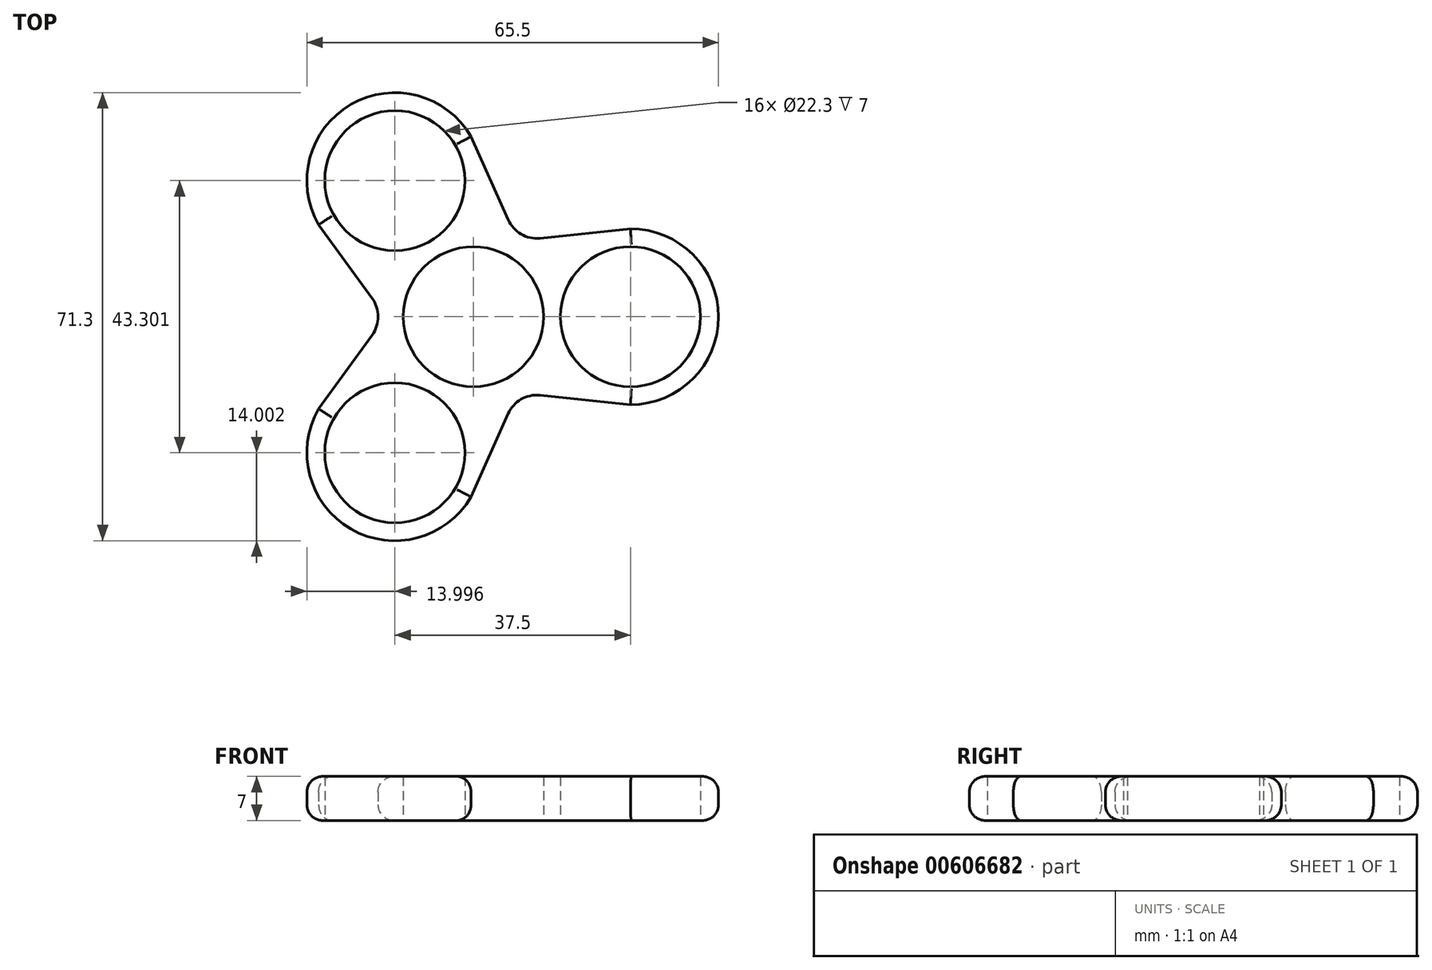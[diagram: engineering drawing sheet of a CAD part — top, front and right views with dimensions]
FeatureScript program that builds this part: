
annotation { "Feature Type Name" : "Feature", "Feature Type Description" : "" }
export const myFeature = defineFeature(function(context is Context, id is Id, definition is map)
    precondition{}
    {
        {
            var Q0;
            Q0=qCreatedBy(makeId("Top.planeOp"),FACE);
            var sketch = newSketch(context, id + "F0", { "sketchPlane" : qUnion([Q0])});
            skCircle(sketch, "E0", {"center": v(-126.34, 8.47) * mm, "radius": 14 * mm});
            skLineSegment(sketch, "E1", {"start": v(-126.34, 8.47) * mm, "end": v(-101.34, 8.47) * mm});
            skLineSegment(sketch, "E2", {"start": v(-126.34, 8.47) * mm, "end": v(-138.84, 30.12) * mm});
            skLineSegment(sketch, "E3", {"start": v(-126.34, 8.47) * mm, "end": v(-138.84, -13.18) * mm});
            skCircle(sketch, "E4", {"center": v(-138.84, 30.12) * mm, "radius": 14 * mm});
            skCircle(sketch, "E5", {"center": v(-101.34, 8.47) * mm, "radius": 14 * mm});
            skCircle(sketch, "E6", {"center": v(-138.84, -13.18) * mm, "radius": 14 * mm});
            skCircle(sketch, "E7", {"center": v(-138.84, 30.12) * mm, "radius": 11.15 * mm});
            skCircle(sketch, "E8", {"center": v(-101.34, 8.47) * mm, "radius": 11.15 * mm});
            skCircle(sketch, "E9", {"center": v(-138.84, -13.18) * mm, "radius": 11.15 * mm});
            skCircle(sketch, "E10", {"center": v(-126.34, 8.47) * mm, "radius": 11.15 * mm});
            skLineSegment(sketch, "E11", {"start": v(-126.34, 8.47) * mm, "end": v(-119.34, -3.65) * mm});
            skLineSegment(sketch, "E12", {"start": v(-126.34, 8.47) * mm, "end": v(-140.34, 8.47) * mm});
            skLineSegment(sketch, "E13", {"start": v(-126.34, 8.47) * mm, "end": v(-119.34, 20.6) * mm});
            skLineSegment(sketch, "E14", {"start": v(-138.84, -13.18) * mm, "end": v(-126.72, -20.18) * mm});
            skLineSegment(sketch, "E15", {"start": v(-138.84, -13.18) * mm, "end": v(-150.97, -6.18) * mm});
            skLineSegment(sketch, "E16", {"start": v(-101.34, 8.47) * mm, "end": v(-101.34, -5.53) * mm});
            skLineSegment(sketch, "E17", {"start": v(-101.34, 8.47) * mm, "end": v(-101.34, 22.47) * mm});
            skLineSegment(sketch, "E18", {"start": v(-138.84, 30.12) * mm, "end": v(-126.72, 37.12) * mm});
            skLineSegment(sketch, "E19", {"start": v(-138.84, 30.12) * mm, "end": v(-150.97, 23.12) * mm});
            skLineSegment(sketch, "E20", {"start": v(-126.72, -20.18) * mm, "end": v(-119.34, -3.65) * mm});
            skLineSegment(sketch, "E21", {"start": v(-150.97, -6.18) * mm, "end": v(-140.34, 8.47) * mm});
            skLineSegment(sketch, "E22", {"start": v(-150.97, 23.12) * mm, "end": v(-140.34, 8.47) * mm});
            skLineSegment(sketch, "E23", {"start": v(-126.72, 37.12) * mm, "end": v(-119.34, 20.6) * mm});
            skLineSegment(sketch, "E24", {"start": v(-101.34, -5.53) * mm, "end": v(-119.34, -3.65) * mm});
            skLineSegment(sketch, "E25", {"start": v(-101.34, 22.47) * mm, "end": v(-119.34, 20.6) * mm});
            skSolve(sketch);
        }
        {
            var Q0;
            {var subQ3=sQuery(id+"F0.wireOp",EDGE,"E19");var subQ5=sQuery(id+"F0.wireOp",EDGE,"E7");var subQ6=makeQuery(id+"F0.imprint","INTERSECT",VERTEX,{"derivedFrom":[subQ5,subQ3]});Q0=makeQuery(id+"F0.imprint","IMPRINT",FACE,{"disambiguationData":[TD([[makeQuery(id+"F0.imprint","IMPRINT",EDGE,{"disambiguationData":[TD([[subQ6,1.0]])],"derivedFrom":subQ5}),-1.0]])]});}
            var Q1;
            {var subQ5=sQuery(id+"F0.wireOp",EDGE,"E23");var subQ6=sQuery(id+"F0.wireOp",EDGE,"E4");var subQ8=makeQuery(id+"F0.imprint","INTERSECT",VERTEX,{"derivedFrom":[subQ6,subQ5]});Q1=makeQuery(id+"F0.imprint","IMPRINT",FACE,{"disambiguationData":[TD([[makeQuery(id+"F0.imprint","IMPRINT",EDGE,{"disambiguationData":[TD([[subQ8,1.0]])],"derivedFrom":subQ6}),1.0]])]});}
            var Q2;
            {var subQ5=sQuery(id+"F0.wireOp",EDGE,"E22");var subQ6=sQuery(id+"F0.wireOp",EDGE,"E4");var subQ8=makeQuery(id+"F0.imprint","INTERSECT",VERTEX,{"derivedFrom":[subQ6,subQ5]});Q2=makeQuery(id+"F0.imprint","IMPRINT",FACE,{"disambiguationData":[TD([[makeQuery(id+"F0.imprint","IMPRINT",EDGE,{"disambiguationData":[TD([[subQ8,-1.0]])],"derivedFrom":subQ6}),1.0]])]});}
            var Q3;
            {var subQ0=sQuery(id+"F0.wireOp",EDGE,"E4");var subQ1=sQuery(id+"F0.wireOp",EDGE,"E0");var subQ2=makeQuery(id+"F0.imprint","INTERSECT",VERTEX,{"disambiguationData":[OD(1.0)],"derivedFrom":[subQ1,subQ0]});Q3=makeQuery(id+"F0.imprint","IMPRINT",FACE,{"disambiguationData":[TD([[makeQuery(id+"F0.imprint","IMPRINT",EDGE,{"disambiguationData":[TD([[subQ2,1.0]])],"derivedFrom":subQ1}),1.0]])]});}
            var Q4;
            {var subQ0=sQuery(id+"F0.wireOp",EDGE,"E4");var subQ1=sQuery(id+"F0.wireOp",EDGE,"E0");var subQ2=makeQuery(id+"F0.imprint","INTERSECT",VERTEX,{"disambiguationData":[OD(0.0)],"derivedFrom":[subQ1,subQ0]});Q4=makeQuery(id+"F0.imprint","IMPRINT",FACE,{"disambiguationData":[TD([[makeQuery(id+"F0.imprint","IMPRINT",EDGE,{"disambiguationData":[TD([[subQ2,-1.0]])],"derivedFrom":subQ1}),1.0]])]});}
            var Q5;
            {var subQ1=sQuery(id+"F0.wireOp",EDGE,"E0");var subQ3=sQuery(id+"F0.wireOp",EDGE,"E4");var subQ4=makeQuery(id+"F0.imprint","INTERSECT",VERTEX,{"disambiguationData":[OD(0.0)],"derivedFrom":[subQ1,subQ3]});Q5=makeQuery(id+"F0.imprint","IMPRINT",FACE,{"disambiguationData":[TD([[makeQuery(id+"F0.imprint","IMPRINT",EDGE,{"disambiguationData":[TD([[subQ4,1.0]])],"derivedFrom":subQ3}),-1.0]])]});}
            var Q6;
            {var subQ1=sQuery(id+"F0.wireOp",EDGE,"E0");var subQ3=sQuery(id+"F0.wireOp",EDGE,"E4");var subQ4=makeQuery(id+"F0.imprint","INTERSECT",VERTEX,{"disambiguationData":[OD(1.0)],"derivedFrom":[subQ1,subQ3]});Q6=makeQuery(id+"F0.imprint","IMPRINT",FACE,{"disambiguationData":[TD([[makeQuery(id+"F0.imprint","IMPRINT",EDGE,{"disambiguationData":[TD([[subQ4,-1.0]])],"derivedFrom":subQ3}),-1.0]])]});}
            var Q7;
            {var subQ1=sQuery(id+"F0.wireOp",EDGE,"E0");var subQ3=sQuery(id+"F0.wireOp",EDGE,"E6");var subQ4=makeQuery(id+"F0.imprint","INTERSECT",VERTEX,{"disambiguationData":[OD(0.0)],"derivedFrom":[subQ1,subQ3]});Q7=makeQuery(id+"F0.imprint","IMPRINT",FACE,{"disambiguationData":[TD([[makeQuery(id+"F0.imprint","IMPRINT",EDGE,{"disambiguationData":[TD([[subQ4,1.0]])],"derivedFrom":subQ3}),-1.0]])]});}
            var Q8;
            {var subQ0=sQuery(id+"F0.wireOp",EDGE,"E21");var subQ2=sQuery(id+"F0.wireOp",EDGE,"E6");var subQ6=makeQuery(id+"F0.imprint","INTERSECT",VERTEX,{"derivedFrom":[subQ2,subQ0]});Q8=makeQuery(id+"F0.imprint","IMPRINT",FACE,{"disambiguationData":[TD([[makeQuery(id+"F0.imprint","IMPRINT",EDGE,{"disambiguationData":[TD([[subQ6,1.0]])],"derivedFrom":subQ2}),1.0]])]});}
            var Q9;
            {var subQ0=sQuery(id+"F0.wireOp",EDGE,"E6");var subQ1=sQuery(id+"F0.wireOp",EDGE,"E0");var subQ2=makeQuery(id+"F0.imprint","INTERSECT",VERTEX,{"disambiguationData":[OD(0.0)],"derivedFrom":[subQ1,subQ0]});Q9=makeQuery(id+"F0.imprint","IMPRINT",FACE,{"disambiguationData":[TD([[makeQuery(id+"F0.imprint","IMPRINT",EDGE,{"disambiguationData":[TD([[subQ2,-1.0]])],"derivedFrom":subQ1}),1.0]])]});}
            var Q10;
            {var subQ0=sQuery(id+"F0.wireOp",EDGE,"E6");var subQ1=sQuery(id+"F0.wireOp",EDGE,"E0");var subQ2=makeQuery(id+"F0.imprint","INTERSECT",VERTEX,{"disambiguationData":[OD(1.0)],"derivedFrom":[subQ1,subQ0]});Q10=makeQuery(id+"F0.imprint","IMPRINT",FACE,{"disambiguationData":[TD([[makeQuery(id+"F0.imprint","IMPRINT",EDGE,{"disambiguationData":[TD([[subQ2,1.0]])],"derivedFrom":subQ1}),1.0]])]});}
            var Q11;
            {var subQ1=sQuery(id+"F0.wireOp",EDGE,"E0");var subQ3=sQuery(id+"F0.wireOp",EDGE,"E6");var subQ4=makeQuery(id+"F0.imprint","INTERSECT",VERTEX,{"disambiguationData":[OD(1.0)],"derivedFrom":[subQ1,subQ3]});Q11=makeQuery(id+"F0.imprint","IMPRINT",FACE,{"disambiguationData":[TD([[makeQuery(id+"F0.imprint","IMPRINT",EDGE,{"disambiguationData":[TD([[subQ4,-1.0]])],"derivedFrom":subQ3}),-1.0]])]});}
            var Q12;
            {var subQ1=sQuery(id+"F0.wireOp",EDGE,"E0");var subQ3=sQuery(id+"F0.wireOp",EDGE,"E5");var subQ4=makeQuery(id+"F0.imprint","INTERSECT",VERTEX,{"disambiguationData":[OD(1.0)],"derivedFrom":[subQ1,subQ3]});Q12=makeQuery(id+"F0.imprint","IMPRINT",FACE,{"disambiguationData":[TD([[makeQuery(id+"F0.imprint","IMPRINT",EDGE,{"disambiguationData":[TD([[subQ4,1.0]])],"derivedFrom":subQ3}),-1.0]])]});}
            var Q13;
            {var subQ0=sQuery(id+"F0.wireOp",EDGE,"E5");var subQ1=sQuery(id+"F0.wireOp",EDGE,"E0");var subQ2=makeQuery(id+"F0.imprint","INTERSECT",VERTEX,{"disambiguationData":[OD(1.0)],"derivedFrom":[subQ1,subQ0]});Q13=makeQuery(id+"F0.imprint","IMPRINT",FACE,{"disambiguationData":[TD([[makeQuery(id+"F0.imprint","IMPRINT",EDGE,{"disambiguationData":[TD([[subQ2,-1.0]])],"derivedFrom":subQ1}),1.0]])]});}
            var Q14;
            {var subQ0=sQuery(id+"F0.wireOp",EDGE,"E5");var subQ1=sQuery(id+"F0.wireOp",EDGE,"E0");var subQ2=makeQuery(id+"F0.imprint","INTERSECT",VERTEX,{"disambiguationData":[OD(0.0)],"derivedFrom":[subQ1,subQ0]});Q14=makeQuery(id+"F0.imprint","IMPRINT",FACE,{"disambiguationData":[TD([[makeQuery(id+"F0.imprint","IMPRINT",EDGE,{"disambiguationData":[TD([[subQ2,1.0]])],"derivedFrom":subQ1}),1.0]])]});}
            var Q15;
            {var subQ1=sQuery(id+"F0.wireOp",EDGE,"E0");var subQ3=sQuery(id+"F0.wireOp",EDGE,"E5");var subQ4=makeQuery(id+"F0.imprint","INTERSECT",VERTEX,{"disambiguationData":[OD(0.0)],"derivedFrom":[subQ1,subQ3]});Q15=makeQuery(id+"F0.imprint","IMPRINT",FACE,{"disambiguationData":[TD([[makeQuery(id+"F0.imprint","IMPRINT",EDGE,{"disambiguationData":[TD([[subQ4,-1.0]])],"derivedFrom":subQ3}),-1.0]])]});}
            var Q16;
            {var subQ0=sQuery(id+"F0.wireOp",EDGE,"E20");var subQ2=sQuery(id+"F0.wireOp",EDGE,"E6");var subQ6=makeQuery(id+"F0.imprint","INTERSECT",VERTEX,{"derivedFrom":[subQ2,subQ0]});Q16=makeQuery(id+"F0.imprint","IMPRINT",FACE,{"disambiguationData":[TD([[makeQuery(id+"F0.imprint","IMPRINT",EDGE,{"disambiguationData":[TD([[subQ6,-1.0]])],"derivedFrom":subQ2}),1.0]])]});}
            var Q17;
            {var subQ3=sQuery(id+"F0.wireOp",EDGE,"E15");var subQ5=sQuery(id+"F0.wireOp",EDGE,"E9");var subQ6=makeQuery(id+"F0.imprint","INTERSECT",VERTEX,{"derivedFrom":[subQ5,subQ3]});Q17=makeQuery(id+"F0.imprint","IMPRINT",FACE,{"disambiguationData":[TD([[makeQuery(id+"F0.imprint","IMPRINT",EDGE,{"disambiguationData":[TD([[subQ6,-1.0]])],"derivedFrom":subQ5}),-1.0]])]});}
            var Q18;
            {var subQ0=sQuery(id+"F0.wireOp",EDGE,"E24");var subQ2=sQuery(id+"F0.wireOp",EDGE,"E5");var subQ8=makeQuery(id+"F0.imprint","INTERSECT",VERTEX,{"derivedFrom":[subQ2,subQ0]});Q18=makeQuery(id+"F0.imprint","IMPRINT",FACE,{"disambiguationData":[TD([[makeQuery(id+"F0.imprint","IMPRINT",EDGE,{"disambiguationData":[TD([[subQ8,1.0]])],"derivedFrom":subQ2}),1.0]])]});}
            var Q19;
            {var subQ0=sQuery(id+"F0.wireOp",EDGE,"E25");var subQ1=sQuery(id+"F0.wireOp",EDGE,"E5");var subQ2=makeQuery(id+"F0.imprint","INTERSECT",VERTEX,{"derivedFrom":[subQ1,subQ0]});Q19=makeQuery(id+"F0.imprint","IMPRINT",FACE,{"disambiguationData":[TD([[makeQuery(id+"F0.imprint","IMPRINT",EDGE,{"disambiguationData":[TD([[subQ2,-1.0]])],"derivedFrom":subQ1}),1.0]])]});}
            var Q20;
            {var subQ3=sQuery(id+"F0.wireOp",EDGE,"E17");var subQ5=sQuery(id+"F0.wireOp",EDGE,"E8");var subQ6=makeQuery(id+"F0.imprint","INTERSECT",VERTEX,{"derivedFrom":[subQ5,subQ3]});Q20=makeQuery(id+"F0.imprint","IMPRINT",FACE,{"disambiguationData":[TD([[makeQuery(id+"F0.imprint","IMPRINT",EDGE,{"disambiguationData":[TD([[subQ6,1.0]])],"derivedFrom":subQ5}),-1.0]])]});}
            var Q21;
            {var subQ0=sQuery(id+"F0.wireOp",EDGE,"E22");var subQ3=sQuery(id+"F0.wireOp",EDGE,"E4");var subQ5=makeQuery(id+"F0.imprint","INTERSECT",VERTEX,{"derivedFrom":[subQ3,subQ0]});Q21=makeQuery(id+"F0.imprint","IMPRINT",FACE,{"disambiguationData":[TD([[makeQuery(id+"F0.imprint","IMPRINT",EDGE,{"disambiguationData":[TD([[subQ5,-1.0]])],"derivedFrom":subQ3}),-1.0]])]});}
            var Q22;
            {var subQ0=sQuery(id+"F0.wireOp",EDGE,"E21");var subQ3=sQuery(id+"F0.wireOp",EDGE,"E6");var subQ5=makeQuery(id+"F0.imprint","INTERSECT",VERTEX,{"derivedFrom":[subQ3,subQ0]});Q22=makeQuery(id+"F0.imprint","IMPRINT",FACE,{"disambiguationData":[TD([[makeQuery(id+"F0.imprint","IMPRINT",EDGE,{"disambiguationData":[TD([[subQ5,1.0]])],"derivedFrom":subQ3}),-1.0]])]});}
            var Q23;
            {var subQ0=sQuery(id+"F0.wireOp",EDGE,"E20");var subQ3=sQuery(id+"F0.wireOp",EDGE,"E6");var subQ5=makeQuery(id+"F0.imprint","INTERSECT",VERTEX,{"derivedFrom":[subQ3,subQ0]});Q23=makeQuery(id+"F0.imprint","IMPRINT",FACE,{"disambiguationData":[TD([[makeQuery(id+"F0.imprint","IMPRINT",EDGE,{"disambiguationData":[TD([[subQ5,-1.0]])],"derivedFrom":subQ3}),-1.0]])]});}
            var Q24;
            {var subQ0=sQuery(id+"F0.wireOp",EDGE,"E24");var subQ3=sQuery(id+"F0.wireOp",EDGE,"E5");var subQ5=makeQuery(id+"F0.imprint","INTERSECT",VERTEX,{"derivedFrom":[subQ3,subQ0]});Q24=makeQuery(id+"F0.imprint","IMPRINT",FACE,{"disambiguationData":[TD([[makeQuery(id+"F0.imprint","IMPRINT",EDGE,{"disambiguationData":[TD([[subQ5,1.0]])],"derivedFrom":subQ3}),-1.0]])]});}
            var Q25;
            {var subQ0=sQuery(id+"F0.wireOp",EDGE,"E25");var subQ3=sQuery(id+"F0.wireOp",EDGE,"E5");var subQ5=makeQuery(id+"F0.imprint","INTERSECT",VERTEX,{"derivedFrom":[subQ3,subQ0]});Q25=makeQuery(id+"F0.imprint","IMPRINT",FACE,{"disambiguationData":[TD([[makeQuery(id+"F0.imprint","IMPRINT",EDGE,{"disambiguationData":[TD([[subQ5,-1.0]])],"derivedFrom":subQ3}),-1.0]])]});}
            var Q26;
            {var subQ0=sQuery(id+"F0.wireOp",EDGE,"E23");var subQ3=sQuery(id+"F0.wireOp",EDGE,"E4");var subQ5=makeQuery(id+"F0.imprint","INTERSECT",VERTEX,{"derivedFrom":[subQ3,subQ0]});Q26=makeQuery(id+"F0.imprint","IMPRINT",FACE,{"disambiguationData":[TD([[makeQuery(id+"F0.imprint","IMPRINT",EDGE,{"disambiguationData":[TD([[subQ5,1.0]])],"derivedFrom":subQ3}),-1.0]])]});}
            extrude(context, id + "F1", {"entities" : qUnion([Q0, Q1, Q2, Q3, Q4, Q5, Q6, Q7, Q8, Q9, Q10, Q11, Q12, Q13, Q14, Q15, Q16, Q17, Q18, Q19, Q20, Q21, Q22, Q23, Q24, Q25, Q26]), "depth" : 7 * mm, "offsetDistance" : 25 * mm});
        }
        {
            var Q0;
            Q0=makeQuery(id+"F1.opExtrude","SWEPT_EDGE",EDGE,{"disambiguationData":[OSD([sQuery(id+"F0.wireOp",EDGE,"E0"),sQuery(id+"F0.wireOp",EDGE,"E11"),sQuery(id+"F0.wireOp",EDGE,"E20"),sQuery(id+"F0.wireOp",EDGE,"E24")])]});
            var Q1;
            Q1=makeQuery(id+"F1.opExtrude","SWEPT_EDGE",EDGE,{"disambiguationData":[OSD([sQuery(id+"F0.wireOp",EDGE,"E0"),sQuery(id+"F0.wireOp",EDGE,"E12"),sQuery(id+"F0.wireOp",EDGE,"E21"),sQuery(id+"F0.wireOp",EDGE,"E22")])]});
            var Q2;
            Q2=makeQuery(id+"F1.opExtrude","SWEPT_EDGE",EDGE,{"disambiguationData":[OSD([sQuery(id+"F0.wireOp",EDGE,"E0"),sQuery(id+"F0.wireOp",EDGE,"E13"),sQuery(id+"F0.wireOp",EDGE,"E23"),sQuery(id+"F0.wireOp",EDGE,"E25")])]});
            fillet(context, id + "F2", {"entities" : qUnion([Q0, Q1, Q2]), "radius" : 5 * mm, "tangentPropagation" : true, "allowEdgeOverflow" : false});
        }
        {
            var Q0;
            Q0=makeQuery(id+"F1.opExtrude","CAP_EDGE",EDGE,{"disambiguationData":[OSD([sQuery(id+"F0.wireOp",EDGE,"E20")])],"isStart":false});
            var Q1;
            Q1=makeQuery(id+"F1.opExtrude","CAP_EDGE",EDGE,{"disambiguationData":[OSD([sQuery(id+"F0.wireOp",EDGE,"E6")])],"isStart":false});
            var Q2;
            Q2=makeQuery(id+"F1.opExtrude","CAP_EDGE",EDGE,{"disambiguationData":[OSD([sQuery(id+"F0.wireOp",EDGE,"E21")])],"isStart":false});
            var Q3;
            {var subQ0=sQuery(id+"F0.wireOp",EDGE,"E22");var subQ1=sQuery(id+"F0.wireOp",EDGE,"E21");Q3=makeQuery(id+"F2.opFillet","BLEND_EDGE",EDGE,{"blendedFrom":[makeQuery(id+"F1.opExtrude","SWEPT_EDGE",EDGE,{"disambiguationData":[OSD([sQuery(id+"F0.wireOp",EDGE,"E0"),sQuery(id+"F0.wireOp",EDGE,"E12"),subQ1,subQ0])]}),makeQuery(id+"F1.opExtrude","CAP_FACE",FACE,{"disambiguationData":[OSD([sQuery(id+"F0.wireOp",EDGE,"E4"),sQuery(id+"F0.wireOp",EDGE,"E5"),sQuery(id+"F0.wireOp",EDGE,"E6"),sQuery(id+"F0.wireOp",EDGE,"E7"),sQuery(id+"F0.wireOp",EDGE,"E8"),sQuery(id+"F0.wireOp",EDGE,"E9"),sQuery(id+"F0.wireOp",EDGE,"E10"),sQuery(id+"F0.wireOp",EDGE,"E20"),subQ1,subQ0,sQuery(id+"F0.wireOp",EDGE,"E23"),sQuery(id+"F0.wireOp",EDGE,"E24"),sQuery(id+"F0.wireOp",EDGE,"E25")])],"isStart":false})],"blendedInto":[makeQuery(id+"F1.opExtrude","CAP_FACE",FACE,{"disambiguationData":[OSD([sQuery(id+"F0.wireOp",EDGE,"E4"),sQuery(id+"F0.wireOp",EDGE,"E5"),sQuery(id+"F0.wireOp",EDGE,"E6"),sQuery(id+"F0.wireOp",EDGE,"E7"),sQuery(id+"F0.wireOp",EDGE,"E8"),sQuery(id+"F0.wireOp",EDGE,"E9"),sQuery(id+"F0.wireOp",EDGE,"E10"),sQuery(id+"F0.wireOp",EDGE,"E20"),subQ1,subQ0,sQuery(id+"F0.wireOp",EDGE,"E23"),sQuery(id+"F0.wireOp",EDGE,"E24"),sQuery(id+"F0.wireOp",EDGE,"E25")])],"isStart":false})]});}
            var Q4;
            Q4=makeQuery(id+"F1.opExtrude","CAP_EDGE",EDGE,{"disambiguationData":[OSD([sQuery(id+"F0.wireOp",EDGE,"E22")])],"isStart":false});
            var Q5;
            Q5=makeQuery(id+"F1.opExtrude","CAP_EDGE",EDGE,{"disambiguationData":[OSD([sQuery(id+"F0.wireOp",EDGE,"E4")])],"isStart":false});
            var Q6;
            Q6=makeQuery(id+"F1.opExtrude","CAP_EDGE",EDGE,{"disambiguationData":[OSD([sQuery(id+"F0.wireOp",EDGE,"E23")])],"isStart":false});
            var Q7;
            Q7=makeQuery(id+"F1.opExtrude","CAP_EDGE",EDGE,{"disambiguationData":[OSD([sQuery(id+"F0.wireOp",EDGE,"E5")])],"isStart":false});
            var Q8;
            Q8=makeQuery(id+"F1.opExtrude","CAP_EDGE",EDGE,{"disambiguationData":[OSD([sQuery(id+"F0.wireOp",EDGE,"E25")])],"isStart":true});
            var Q9;
            Q9=makeQuery(id+"F1.opExtrude","CAP_EDGE",EDGE,{"disambiguationData":[OSD([sQuery(id+"F0.wireOp",EDGE,"E4")])],"isStart":true});
            var Q10;
            {var subQ0=sQuery(id+"F0.wireOp",EDGE,"E22");var subQ1=sQuery(id+"F0.wireOp",EDGE,"E21");Q10=makeQuery(id+"F2.opFillet","BLEND_EDGE",EDGE,{"blendedFrom":[makeQuery(id+"F1.opExtrude","SWEPT_EDGE",EDGE,{"disambiguationData":[OSD([sQuery(id+"F0.wireOp",EDGE,"E0"),sQuery(id+"F0.wireOp",EDGE,"E12"),subQ1,subQ0])]}),makeQuery(id+"F1.opExtrude","CAP_FACE",FACE,{"disambiguationData":[OSD([sQuery(id+"F0.wireOp",EDGE,"E4"),sQuery(id+"F0.wireOp",EDGE,"E5"),sQuery(id+"F0.wireOp",EDGE,"E6"),sQuery(id+"F0.wireOp",EDGE,"E7"),sQuery(id+"F0.wireOp",EDGE,"E8"),sQuery(id+"F0.wireOp",EDGE,"E9"),sQuery(id+"F0.wireOp",EDGE,"E10"),sQuery(id+"F0.wireOp",EDGE,"E20"),subQ1,subQ0,sQuery(id+"F0.wireOp",EDGE,"E23"),sQuery(id+"F0.wireOp",EDGE,"E24"),sQuery(id+"F0.wireOp",EDGE,"E25")])],"isStart":true})],"blendedInto":[makeQuery(id+"F1.opExtrude","CAP_FACE",FACE,{"disambiguationData":[OSD([sQuery(id+"F0.wireOp",EDGE,"E4"),sQuery(id+"F0.wireOp",EDGE,"E5"),sQuery(id+"F0.wireOp",EDGE,"E6"),sQuery(id+"F0.wireOp",EDGE,"E7"),sQuery(id+"F0.wireOp",EDGE,"E8"),sQuery(id+"F0.wireOp",EDGE,"E9"),sQuery(id+"F0.wireOp",EDGE,"E10"),sQuery(id+"F0.wireOp",EDGE,"E20"),subQ1,subQ0,sQuery(id+"F0.wireOp",EDGE,"E23"),sQuery(id+"F0.wireOp",EDGE,"E24"),sQuery(id+"F0.wireOp",EDGE,"E25")])],"isStart":true})]});}
            var Q11;
            Q11=makeQuery(id+"F1.opExtrude","CAP_EDGE",EDGE,{"disambiguationData":[OSD([sQuery(id+"F0.wireOp",EDGE,"E6")])],"isStart":true});
            var Q12;
            Q12=makeQuery(id+"F1.opExtrude","CAP_EDGE",EDGE,{"disambiguationData":[OSD([sQuery(id+"F0.wireOp",EDGE,"E20")])],"isStart":true});
            var Q13;
            Q13=makeQuery(id+"F1.opExtrude","CAP_EDGE",EDGE,{"disambiguationData":[OSD([sQuery(id+"F0.wireOp",EDGE,"E5")])],"isStart":true});
            fillet(context, id + "F3", {"entities" : qUnion([Q0, Q1, Q2, Q3, Q4, Q5, Q6, Q7, Q8, Q9, Q10, Q11, Q12, Q13]), "radius" : 2.5 * mm, "tangentPropagation" : true, "allowEdgeOverflow" : false});
        }
    });
